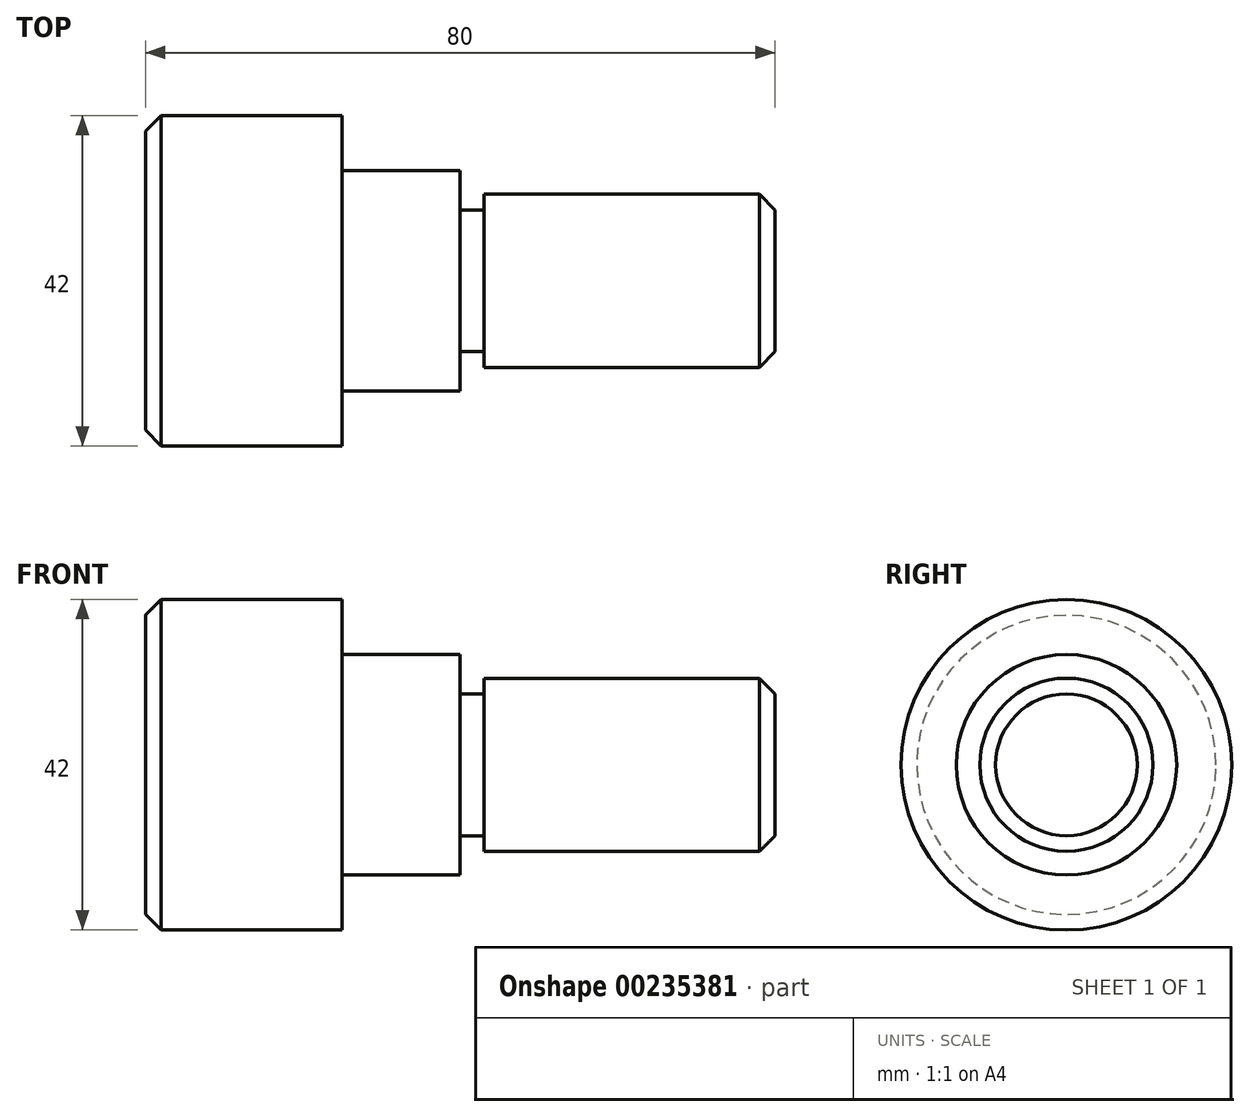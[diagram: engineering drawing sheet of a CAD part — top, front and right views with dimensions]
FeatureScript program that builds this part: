
annotation { "Feature Type Name" : "Feature", "Feature Type Description" : "" }
export const myFeature = defineFeature(function(context is Context, id is Id, definition is map)
    precondition{}
    {
        {
            var Q0;
            Q0=qCreatedBy(makeId("Front.planeOp"),FACE);
            var sketch = newSketch(context, id + "F0", { "sketchPlane" : qUnion([Q0])});
            skLineSegment(sketch, "E0", {"start": v(-41.54, 0) * mm, "end": v(-41.54, 21) * mm});
            skLineSegment(sketch, "E1", {"start": v(-41.54, 21) * mm, "end": v(-16.54, 21) * mm});
            skLineSegment(sketch, "E2", {"start": v(-16.54, 21) * mm, "end": v(-16.54, 14) * mm});
            skLineSegment(sketch, "E3", {"start": v(-16.54, 14) * mm, "end": v(-1.54, 14) * mm});
            skLineSegment(sketch, "E4", {"start": v(-1.54, 14) * mm, "end": v(-1.54, 9) * mm});
            skLineSegment(sketch, "E5", {"start": v(-1.54, 9) * mm, "end": v(1.46, 9) * mm});
            skLineSegment(sketch, "E6", {"start": v(1.46, 9) * mm, "end": v(1.46, 11) * mm});
            skLineSegment(sketch, "E7", {"start": v(38.46, 11) * mm, "end": v(38.46, 0) * mm});
            skLineSegment(sketch, "E8", {"start": v(38.46, 0) * mm, "end": v(-41.54, 0) * mm});
            skLineSegment(sketch, "E9", {"start": v(38.46, 11) * mm, "end": v(1.46, 11) * mm});
            skLineSegment(sketch, "E10", {"start": v(-63.42, 0) * mm, "end": v(67.26, 0) * mm, "construction": true});
            skLineSegment(sketch, "E11", {"start": v(-41.54, 0) * mm, "end": v(38.46, 0) * mm});
            skLineSegment(sketch, "E12", {"start": v(38.46, 0) * mm, "end": v(38.46, 11) * mm});
            skSolve(sketch);
        }
        {
            var Q0;
            Q0=makeQuery(id+"F0.imprint","IMPRINT",FACE,{"disambiguationData":[TD([[makeQuery(id+"F0.imprint","IMPRINT",EDGE,{"derivedFrom":sQuery(id+"F0.wireOp",EDGE,"E0")}),-1.0]])]});
            var Q1;
            Q1=sQuery(id+"F0.wireOp",EDGE,"E0");
            var Q2;
            Q2=sQuery(id+"F0.wireOp",EDGE,"E3");
            var Q3;
            Q3=sQuery(id+"F0.wireOp",EDGE,"E7");
            var Q4;
            Q4=sQuery(id+"F0.wireOp",EDGE,"E1");
            var Q5;
            Q5=sQuery(id+"F0.wireOp",EDGE,"E9");
            var Q6;
            Q6=sQuery(id+"F0.wireOp",EDGE,"E2");
            var Q7;
            Q7=sQuery(id+"F0.wireOp",EDGE,"E5");
            var Q8;
            Q8=sQuery(id+"F0.wireOp",EDGE,"E4");
            var Q9;
            Q9=sQuery(id+"F0.wireOp",EDGE,"E6");
            var Q10;
            Q10=sQuery(id+"F0.wireOp",EDGE,"E10");
            revolve(context, id + "F1", {"bodyType" : ToolBodyType.SURFACE, "operationType" : NewBodyOperationType.ADD, "entities" : qUnion([Q0]), "surfaceEntities" : qUnion([Q1, Q2, Q3, Q4, Q5, Q6, Q7, Q8, Q9]), "axis" : qUnion([Q10]), "revolveType" : RevolveType.FULL, "oppositeDirection" : true});
        }
        {
            var Q0;
            Q0=makeQuery(id+"F1.opRevolve","SWEPT_EDGE",EDGE,{"disambiguationData":[OSD([sQuery(id+"F0.wireOp",VERTEX,"E9.start")])]});
            var Q1;
            Q1=makeQuery(id+"F1.opRevolve","SWEPT_EDGE",EDGE,{"disambiguationData":[OSD([sQuery(id+"F0.wireOp",VERTEX,"E1.start")])]});
            chamfer(context, id + "F2", {"entities" : qUnion([Q0, Q1]), "chamferType" : ChamferType.OFFSET_ANGLE, "width" : 2 * mm, "oppositeDirection" : false, "angle" : 45 * degree, "tangentPropagation" : true});
        }
    });
